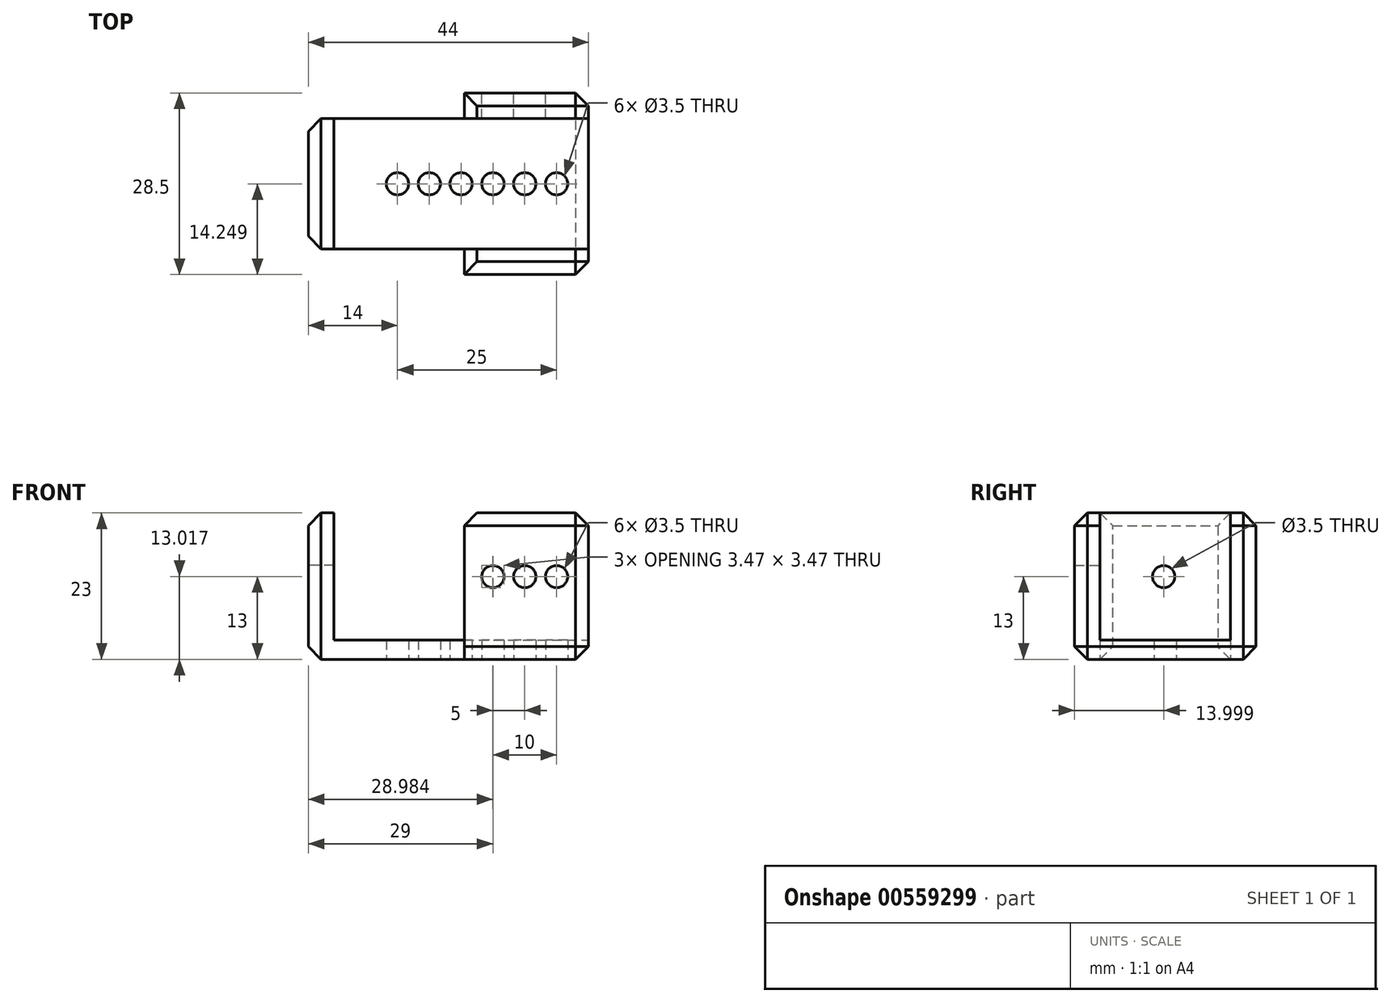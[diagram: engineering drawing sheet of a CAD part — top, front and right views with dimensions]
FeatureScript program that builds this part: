
annotation { "Feature Type Name" : "Feature", "Feature Type Description" : "" }
export const myFeature = defineFeature(function(context is Context, id is Id, definition is map)
    precondition{}
    {
        {
            var Q0;
            Q0=qCreatedBy(makeId("Top.planeOp"),FACE);
            var sketch = newSketch(context, id + "F0", { "sketchPlane" : qUnion([Q0])});
            skLineSegment(sketch, "E0", {"start": v(-54.8, 23.52) * mm, "end": v(-54.8, 3.02) * mm});
            skLineSegment(sketch, "E1", {"start": v(-54.8, 23.52) * mm, "end": v(-14.8, 23.52) * mm});
            skLineSegment(sketch, "E2", {"start": v(-54.8, 3.02) * mm, "end": v(-14.8, 3.02) * mm});
            skLineSegment(sketch, "E3", {"start": v(-14.8, 3.02) * mm, "end": v(-14.8, 23.52) * mm});
            skLineSegment(sketch, "E4", {"start": v(-58.8, 3.02) * mm, "end": v(-54.8, 3.02) * mm});
            skLineSegment(sketch, "E5", {"start": v(-14.8, 23.52) * mm, "end": v(-14.8, 27.52) * mm});
            skLineSegment(sketch, "E6", {"start": v(-14.8, 27.52) * mm, "end": v(-58.8, 27.52) * mm});
            skLineSegment(sketch, "E7", {"start": v(-58.8, 27.52) * mm, "end": v(-58.8, 3.02) * mm});
            skLineSegment(sketch, "E8", {"start": v(-54.8, 23.52) * mm, "end": v(-34.8, 3.02) * mm, "construction": true});
            skLineSegment(sketch, "E9", {"start": v(-34.8, 3.02) * mm, "end": v(-14.8, 23.52) * mm, "construction": true});
            skLineSegment(sketch, "E10", {"start": v(-14.8, 3.02) * mm, "end": v(-34.8, 23.52) * mm, "construction": true});
            skLineSegment(sketch, "E11", {"start": v(-34.8, 23.52) * mm, "end": v(-54.8, 3.02) * mm, "construction": true});
            skCircle(sketch, "E12", {"center": v(-24.8, 13.27) * mm, "radius": 1.75 * mm});
            skLineSegment(sketch, "E13", {"start": v(-24.8, 13.27) * mm, "end": v(-29.8, 13.27) * mm});
            skLineSegment(sketch, "E14", {"start": v(-29.8, 13.27) * mm, "end": v(-34.8, 13.27) * mm});
            skLineSegment(sketch, "E15", {"start": v(-34.8, 13.27) * mm, "end": v(-39.8, 13.27) * mm});
            skLineSegment(sketch, "E16", {"start": v(-39.8, 13.27) * mm, "end": v(-44.8, 13.27) * mm});
            skLineSegment(sketch, "E17", {"start": v(-24.8, 13.27) * mm, "end": v(-19.8, 13.27) * mm});
            skLineSegment(sketch, "E18", {"start": v(-19.8, 13.27) * mm, "end": v(-14.8, 13.27) * mm});
            skCircle(sketch, "E19", {"center": v(-39.8, 13.27) * mm, "radius": 1.75 * mm});
            skCircle(sketch, "E20", {"center": v(-34.8, 13.27) * mm, "radius": 1.75 * mm});
            skCircle(sketch, "E21", {"center": v(-19.8, 13.27) * mm, "radius": 1.75 * mm});
            skCircle(sketch, "E22", {"center": v(-29.8, 13.27) * mm, "radius": 1.75 * mm});
            skCircle(sketch, "E23", {"center": v(-44.8, 13.27) * mm, "radius": 1.75 * mm});
            skLineSegment(sketch, "E24", {"start": v(-14.8, 3.02) * mm, "end": v(-14.8, -0.98) * mm});
            skLineSegment(sketch, "E25", {"start": v(-14.8, -0.98) * mm, "end": v(-34.3, -0.98) * mm});
            skLineSegment(sketch, "E26", {"start": v(-34.3, -0.98) * mm, "end": v(-34.3, 3.02) * mm});
            skLineSegment(sketch, "E27", {"start": v(-34.3, 3.02) * mm, "end": v(-34.3, 27.52) * mm});
            skLineSegment(sketch, "E28", {"start": v(-54.8, 23.52) * mm, "end": v(-58.8, 23.52) * mm});
            skSolve(sketch);
        }
        {
            var Q0;
            Q0=makeQuery(id+"F0.imprint","IMPRINT",FACE,{"disambiguationData":[TD([[makeQuery(id+"F0.imprint","IMPRINT",EDGE,{"derivedFrom":sQuery(id+"F0.wireOp",EDGE,"E0")}),1.0]])]});
            var Q1;
            {var subQ5=sQuery(id+"F0.wireOp",EDGE,"E13");var subQ6=sQuery(id+"F0.wireOp",EDGE,"E12");var subQ7=makeQuery(id+"F0.imprint","INTERSECT",VERTEX,{"derivedFrom":[subQ6,subQ5]});Q1=makeQuery(id+"F0.imprint","IMPRINT",FACE,{"disambiguationData":[TD([[makeQuery(id+"F0.imprint","IMPRINT",EDGE,{"disambiguationData":[TD([[subQ7,1.0]])],"derivedFrom":subQ6}),-1.0]])]});}
            var Q2;
            {var subQ1=sQuery(id+"F0.wireOp",EDGE,"E13");var subQ5=sQuery(id+"F0.wireOp",EDGE,"E12");var subQ6=makeQuery(id+"F0.imprint","INTERSECT",VERTEX,{"derivedFrom":[subQ5,subQ1]});Q2=makeQuery(id+"F0.imprint","IMPRINT",FACE,{"disambiguationData":[TD([[makeQuery(id+"F0.imprint","IMPRINT",EDGE,{"disambiguationData":[TD([[subQ6,-1.0]])],"derivedFrom":subQ5}),-1.0]])]});}
            extrude(context, id + "F1", {"entities" : qUnion([Q0, Q1, Q2]), "depth" : 3 * mm, "offsetDistance" : 25 * mm});
        }
        {
            var Q0;
            Q0=makeQuery(id+"F0.imprint","IMPRINT",FACE,{"disambiguationData":[TD([[makeQuery(id+"F0.imprint","IMPRINT",EDGE,{"derivedFrom":sQuery(id+"F0.wireOp",EDGE,"E0")}),-1.0]])]});
            var Q1;
            {var subQ0=sQuery(id+"F0.wireOp",EDGE,"E24");Q1=makeQuery(id+"F0.imprint","IMPRINT",FACE,{"disambiguationData":[TD([[makeQuery(id+"F0.imprint","IMPRINT",EDGE,{"derivedFrom":subQ0}),-1.0]])]});}
            var Q2;
            {var subQ0=sQuery(id+"F0.wireOp",EDGE,"E5");Q2=makeQuery(id+"F0.imprint","IMPRINT",FACE,{"disambiguationData":[TD([[makeQuery(id+"F0.imprint","IMPRINT",EDGE,{"derivedFrom":subQ0}),1.0]])]});}
            extrude(context, id + "F2", {"entities" : qUnion([Q0, Q1, Q2]), "operationType" : NewBodyOperationType.ADD, "depth" : 23 * mm, "offsetDistance" : 25 * mm});
        }
        {
            var Q0;
            Q0=makeQuery(id+"F2.opExtrude","SWEPT_FACE",FACE,{"disambiguationData":[OSD([sQuery(id+"F0.wireOp",EDGE,"E6")])]});
            var sketch = newSketch(context, id + "F3", { "sketchPlane" : qUnion([Q0])});
            skLineSegment(sketch, "E29.bottom", {"start": v(14.8, 23) * mm, "end": v(58.8, 23) * mm});
            skLineSegment(sketch, "E29.top", {"start": v(14.8, 3) * mm, "end": v(58.8, 3) * mm});
            skLineSegment(sketch, "E29.left", {"start": v(14.8, 23) * mm, "end": v(14.8, 3) * mm});
            skLineSegment(sketch, "E29.right", {"start": v(58.8, 23) * mm, "end": v(58.8, 3) * mm});
            skLineSegment(sketch, "E30", {"start": v(49.8, 13) * mm, "end": v(44.8, 13) * mm, "construction": true});
            skLineSegment(sketch, "E31", {"start": v(44.8, 13) * mm, "end": v(39.8, 13) * mm, "construction": true});
            skLineSegment(sketch, "E32", {"start": v(39.8, 13) * mm, "end": v(34.8, 13) * mm, "construction": true});
            skLineSegment(sketch, "E33", {"start": v(34.8, 13) * mm, "end": v(29.8, 13) * mm, "construction": true});
            skLineSegment(sketch, "E34", {"start": v(29.8, 13) * mm, "end": v(24.8, 13) * mm, "construction": true});
            skLineSegment(sketch, "E35", {"start": v(24.8, 13) * mm, "end": v(19.8, 13) * mm, "construction": true});
            skCircle(sketch, "E36", {"center": v(19.8, 13) * mm, "radius": 1.75 * mm});
            skCircle(sketch, "E37", {"center": v(24.8, 13) * mm, "radius": 1.75 * mm});
            skCircle(sketch, "E38", {"center": v(29.8, 13) * mm, "radius": 1.75 * mm});
            skCircle(sketch, "E39", {"center": v(34.8, 13) * mm, "radius": 1.75 * mm});
            skCircle(sketch, "E40", {"center": v(39.8, 13) * mm, "radius": 1.75 * mm});
            skCircle(sketch, "E41", {"center": v(44.8, 13) * mm, "radius": 1.75 * mm});
            skCircle(sketch, "E42", {"center": v(49.8, 13) * mm, "radius": 1.75 * mm});
            skLineSegment(sketch, "E43", {"start": v(14.8, 13) * mm, "end": v(19.8, 13) * mm, "construction": true});
            skSolve(sketch);
        }
        {
            var Q0;
            Q0=makeQuery(id+"F3.imprint","IMPRINT",FACE,{"disambiguationData":[TD([[makeQuery(id+"F3.imprint","IMPRINT",EDGE,{"derivedFrom":sQuery(id+"F3.wireOp",EDGE,"E36")}),1.0]])]});
            var Q1;
            Q1=makeQuery(id+"F3.imprint","IMPRINT",FACE,{"disambiguationData":[TD([[makeQuery(id+"F3.imprint","IMPRINT",EDGE,{"derivedFrom":sQuery(id+"F3.wireOp",EDGE,"E37")}),1.0]])]});
            var Q2;
            Q2=makeQuery(id+"F3.imprint","IMPRINT",FACE,{"disambiguationData":[TD([[makeQuery(id+"F3.imprint","IMPRINT",EDGE,{"derivedFrom":sQuery(id+"F3.wireOp",EDGE,"E38")}),1.0]])]});
            var Q3;
            Q3=makeQuery(id+"F3.imprint","IMPRINT",FACE,{"disambiguationData":[TD([[makeQuery(id+"F3.imprint","IMPRINT",EDGE,{"derivedFrom":sQuery(id+"F3.wireOp",EDGE,"E40")}),1.0]])]});
            var Q4;
            Q4=makeQuery(id+"F3.imprint","IMPRINT",FACE,{"disambiguationData":[TD([[makeQuery(id+"F3.imprint","IMPRINT",EDGE,{"derivedFrom":sQuery(id+"F3.wireOp",EDGE,"E41")}),1.0]])]});
            var Q5;
            Q5=makeQuery(id+"F3.imprint","IMPRINT",FACE,{"disambiguationData":[TD([[makeQuery(id+"F3.imprint","IMPRINT",EDGE,{"derivedFrom":sQuery(id+"F3.wireOp",EDGE,"E42")}),1.0]])]});
            extrude(context, id + "F4", {"entities" : qUnion([Q0, Q1, Q2, Q3, Q4, Q5]), "operationType" : NewBodyOperationType.REMOVE, "endBound" : BoundingType.THROUGH_ALL, "oppositeDirection" : true, "depth" : 25 * mm, "offsetDistance" : 25 * mm});
        }
        {
            var Q0;
            Q0=makeQuery(id+"F2.opExtrude","SWEPT_FACE",FACE,{"disambiguationData":[OSD([sQuery(id+"F0.wireOp",EDGE,"E7")])]});
            var sketch = newSketch(context, id + "F5", { "sketchPlane" : qUnion([Q0])});
            skLineSegment(sketch, "E44.bottom", {"start": v(-3.02, 23) * mm, "end": v(-23.02, 23) * mm});
            skLineSegment(sketch, "E44.top", {"start": v(-3.02, 3) * mm, "end": v(-23.02, 3) * mm});
            skLineSegment(sketch, "E44.left", {"start": v(-3.02, 23) * mm, "end": v(-3.02, 3) * mm});
            skLineSegment(sketch, "E44.right", {"start": v(-23.02, 23) * mm, "end": v(-23.02, 3) * mm});
            skLineSegment(sketch, "E45", {"start": v(-23.02, 3) * mm, "end": v(-3.02, 23) * mm});
            skLineSegment(sketch, "E46", {"start": v(-3.02, 3) * mm, "end": v(-23.02, 23) * mm});
            skCircle(sketch, "E47", {"center": v(-13.02, 13) * mm, "radius": 1.75 * mm});
            skSolve(sketch);
        }
        {
            var Q0;
            {var subQ0=sQuery(id+"F5.wireOp",EDGE,"E46");var subQ1=sQuery(id+"F5.wireOp",EDGE,"E45");var subQ2=makeQuery(id+"F5.imprint","INTERSECT",VERTEX,{"derivedFrom":[subQ1,subQ0]});Q0=makeQuery(id+"F5.imprint","IMPRINT",FACE,{"disambiguationData":[TD([[makeQuery(id+"F5.imprint","IMPRINT",EDGE,{"disambiguationData":[TD([[subQ2,-1.0]])],"derivedFrom":subQ1}),1.0]])]});}
            var Q1;
            {var subQ0=sQuery(id+"F5.wireOp",EDGE,"E47");var subQ1=sQuery(id+"F5.wireOp",EDGE,"E45");var subQ2=makeQuery(id+"F5.imprint","INTERSECT",VERTEX,{"disambiguationData":[OD(0.0)],"derivedFrom":[subQ1,subQ0]});Q1=makeQuery(id+"F5.imprint","IMPRINT",FACE,{"disambiguationData":[TD([[makeQuery(id+"F5.imprint","IMPRINT",EDGE,{"disambiguationData":[TD([[subQ2,-1.0]])],"derivedFrom":subQ1}),-1.0]])]});}
            var Q2;
            {var subQ0=sQuery(id+"F5.wireOp",EDGE,"E46");var subQ1=sQuery(id+"F5.wireOp",EDGE,"E45");var subQ2=makeQuery(id+"F5.imprint","INTERSECT",VERTEX,{"derivedFrom":[subQ1,subQ0]});Q2=makeQuery(id+"F5.imprint","IMPRINT",FACE,{"disambiguationData":[TD([[makeQuery(id+"F5.imprint","IMPRINT",EDGE,{"disambiguationData":[TD([[subQ2,-1.0]])],"derivedFrom":subQ1}),-1.0]])]});}
            var Q3;
            {var subQ0=sQuery(id+"F5.wireOp",EDGE,"E47");var subQ1=sQuery(id+"F5.wireOp",EDGE,"E45");var subQ2=makeQuery(id+"F5.imprint","INTERSECT",VERTEX,{"disambiguationData":[OD(0.0)],"derivedFrom":[subQ1,subQ0]});Q3=makeQuery(id+"F5.imprint","IMPRINT",FACE,{"disambiguationData":[TD([[makeQuery(id+"F5.imprint","IMPRINT",EDGE,{"disambiguationData":[TD([[subQ2,-1.0]])],"derivedFrom":subQ1}),1.0]])]});}
            extrude(context, id + "F6", {"entities" : qUnion([Q0, Q1, Q2, Q3]), "operationType" : NewBodyOperationType.REMOVE, "oppositeDirection" : true, "depth" : 25 * mm, "offsetDistance" : 25 * mm});
        }
        {
            var Q0;
            Q0=makeQuery(id+"F2.opExtrude","CAP_EDGE",EDGE,{"disambiguationData":[OSD([sQuery(id+"F0.wireOp",EDGE,"E25")])],"isStart":false});
            var Q1;
            Q1=makeQuery(id+"F2.opExtrude","SWEPT_EDGE",EDGE,{"disambiguationData":[OSD([sQuery(id+"F0.wireOp",EDGE,"E24"),sQuery(id+"F0.wireOp",EDGE,"E25")])]});
            var Q2;
            Q2=makeQuery(id+"F2.opExtrude","CAP_EDGE",EDGE,{"disambiguationData":[OSD([sQuery(id+"F0.wireOp",EDGE,"E25")])],"isStart":true});
            var Q3;
            Q3=makeQuery(id+"F2.boolean.opBoolean","MERGE",EDGE,{"derivedFrom":[makeQuery(id+"F1.opExtrude","CAP_EDGE",EDGE,{"disambiguationData":[OSD([sQuery(id+"F0.wireOp",EDGE,"E3")])],"isStart":true}),makeQuery(id+"F2.opExtrude","CAP_EDGE",EDGE,{"disambiguationData":[OSD([sQuery(id+"F0.wireOp",EDGE,"E5")])],"isStart":true}),makeQuery(id+"F2.opExtrude","CAP_EDGE",EDGE,{"disambiguationData":[OSD([sQuery(id+"F0.wireOp",EDGE,"E24")])],"isStart":true})]});
            var Q4;
            Q4=makeQuery(id+"F2.opExtrude","SWEPT_EDGE",EDGE,{"disambiguationData":[OSD([sQuery(id+"F0.wireOp",EDGE,"E5"),sQuery(id+"F0.wireOp",EDGE,"E6")])]});
            var Q5;
            Q5=makeQuery(id+"F2.opExtrude","CAP_EDGE",EDGE,{"disambiguationData":[OSD([sQuery(id+"F0.wireOp",EDGE,"E24")])],"isStart":false});
            var Q6;
            Q6=makeQuery(id+"F2.opExtrude","CAP_EDGE",EDGE,{"disambiguationData":[OSD([sQuery(id+"F0.wireOp",EDGE,"E5")])],"isStart":false});
            var Q7;
            Q7=makeQuery(id+"F2.opExtrude","CAP_EDGE",EDGE,{"disambiguationData":[OSD([sQuery(id+"F0.wireOp",EDGE,"E6")])],"isStart":false});
            var Q8;
            Q8=makeQuery(id+"F2.opExtrude","CAP_EDGE",EDGE,{"disambiguationData":[OSD([sQuery(id+"F0.wireOp",EDGE,"E27")])],"isStart":false});
            var Q9;
            Q9=makeQuery(id+"F2.opExtrude","CAP_EDGE",EDGE,{"disambiguationData":[OSD([sQuery(id+"F0.wireOp",EDGE,"E26")])],"isStart":false});
            var Q10;
            Q10=makeQuery(id+"F2.opExtrude","CAP_EDGE",EDGE,{"disambiguationData":[OSD([sQuery(id+"F0.wireOp",EDGE,"E6")])],"isStart":true});
            var Q11;
            Q11=makeQuery(id+"F2.opExtrude","SWEPT_EDGE",EDGE,{"disambiguationData":[OSD([sQuery(id+"F0.wireOp",EDGE,"E7"),sQuery(id+"F0.wireOp",EDGE,"E28")])]});
            var Q12;
            Q12=makeQuery(id+"F2.opExtrude","SWEPT_EDGE",EDGE,{"disambiguationData":[OSD([sQuery(id+"F0.wireOp",EDGE,"E4"),sQuery(id+"F0.wireOp",EDGE,"E7")])]});
            var Q13;
            Q13=makeQuery(id+"F2.opExtrude","CAP_EDGE",EDGE,{"disambiguationData":[OSD([sQuery(id+"F0.wireOp",EDGE,"E7")])],"isStart":false});
            var Q14;
            Q14=makeQuery(id+"F2.opExtrude","CAP_EDGE",EDGE,{"disambiguationData":[OSD([sQuery(id+"F0.wireOp",EDGE,"E7")])],"isStart":true});
            chamfer(context, id + "F7", {"entities" : qUnion([Q0, Q1, Q2, Q3, Q4, Q5, Q6, Q7, Q8, Q9, Q10, Q11, Q12, Q13, Q14]), "width" : 2 * mm, "tangentPropagation" : true});
        }
    });
